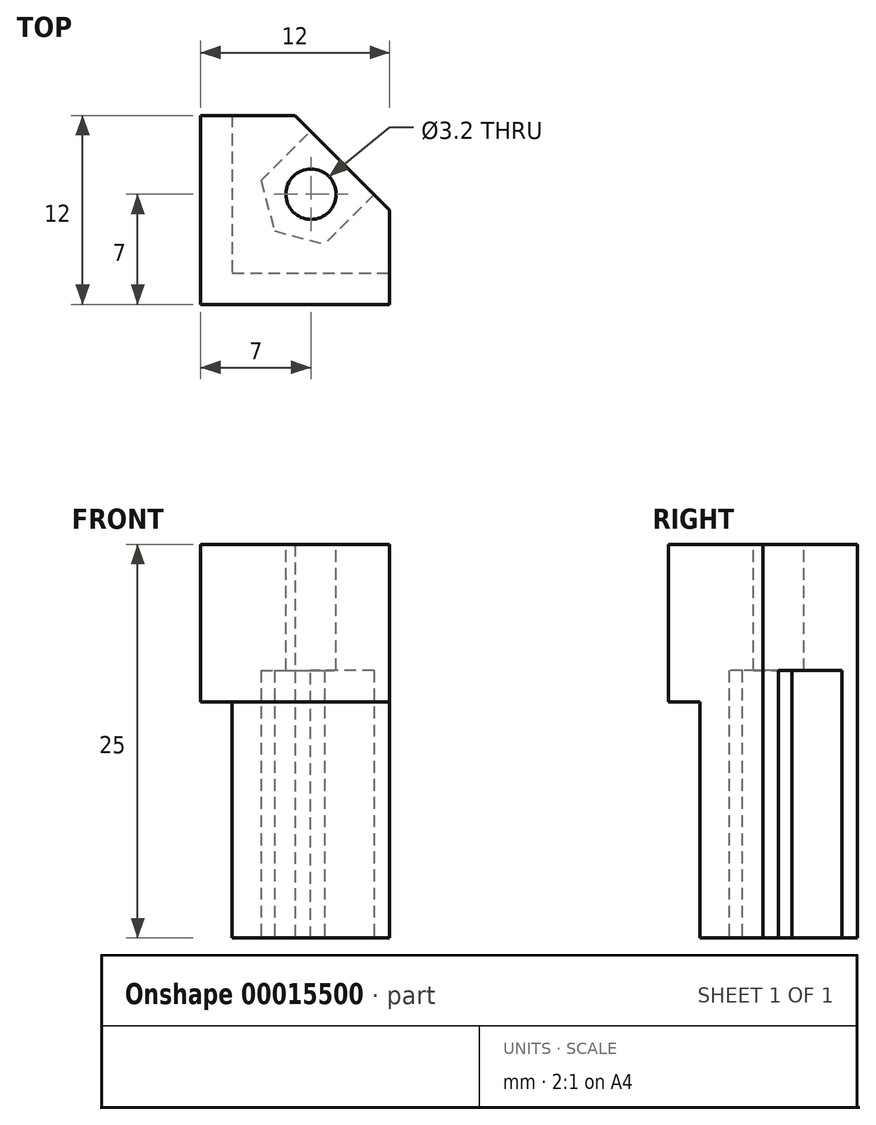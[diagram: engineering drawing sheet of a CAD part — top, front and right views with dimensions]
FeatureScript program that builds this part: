
annotation { "Feature Type Name" : "Feature", "Feature Type Description" : "" }
export const myFeature = defineFeature(function(context is Context, id is Id, definition is map)
    precondition{}
    {
        {
            var Q0;
            Q0=qCreatedBy(makeId("Top.planeOp"),FACE);
            var sketch = newSketch(context, id + "F0", { "sketchPlane" : qUnion([Q0])});
            skLineSegment(sketch, "E0", {"start": v(0, 0) * mm, "end": v(0, 12) * mm});
            skLineSegment(sketch, "E1", {"start": v(0, 12) * mm, "end": v(6, 12) * mm});
            skLineSegment(sketch, "E2", {"start": v(6, 12) * mm, "end": v(12, 6) * mm});
            skLineSegment(sketch, "E3", {"start": v(12, 6) * mm, "end": v(12, 0) * mm});
            skLineSegment(sketch, "E4", {"start": v(12, 0) * mm, "end": v(0, 0) * mm});
            skSolve(sketch);
        }
        {
            var Q0;
            Q0 = qSketchRegion(id + "F0", true);
            extrude(context, id + "F1", {"entities" : qUnion([Q0]), "depth" : 10 * mm});
        }
        {
            var Q0;
            Q0=qCreatedBy(makeId("Top.planeOp"),FACE);
            var sketch = newSketch(context, id + "F2", { "sketchPlane" : qUnion([Q0])});
            skLineSegment(sketch, "E5", {"start": v(2, 12) * mm, "end": v(2, 2) * mm});
            skLineSegment(sketch, "E6", {"start": v(2, 2) * mm, "end": v(12, 2) * mm});
            skLineSegment(sketch, "E7", {"start": v(12, 2) * mm, "end": v(2, 12) * mm, "construction": true});
            skLineSegment(sketch, "E8", {"start": v(12, 2) * mm, "end": v(12, 6) * mm});
            skLineSegment(sketch, "E9", {"start": v(12, 6) * mm, "end": v(6, 12) * mm});
            skLineSegment(sketch, "E10", {"start": v(6, 12) * mm, "end": v(2, 12) * mm});
            skSolve(sketch);
        }
        {
            var Q0;
            Q0 = qSketchRegion(id + "F2", true);
            extrude(context, id + "F3", {"entities" : qUnion([Q0]), "operationType" : NewBodyOperationType.ADD, "oppositeDirection" : true, "depth" : 15 * mm});
        }
        {
            var Q0;
            Q0=makeQuery(id+"F1.opExtrude","CAP_FACE",FACE,{"disambiguationData":[OSD([sQuery(id+"F0.wireOp",EDGE,"E0"),sQuery(id+"F0.wireOp",EDGE,"E1"),sQuery(id+"F0.wireOp",EDGE,"E2"),sQuery(id+"F0.wireOp",EDGE,"E3"),sQuery(id+"F0.wireOp",EDGE,"E4")])],"isStart":false});
            var sketch = newSketch(context, id + "F4", { "sketchPlane" : qUnion([Q0])});
            skPoint(sketch, "E11", {"position": v(7, 7) * mm});
            skSolve(sketch);
        }
        {
            var Q0;
            Q0=sQuery(id+"F4.wireOp",VERTEX,"E11");
            var Q1;
            Q1=makeQuery(id+"F1.opExtrude","SWEPT_BODY",BODY,{"disambiguationData":[OSD([sQuery(id+"F0.wireOp",EDGE,"E0"),sQuery(id+"F0.wireOp",EDGE,"E1"),sQuery(id+"F0.wireOp",EDGE,"E2"),sQuery(id+"F0.wireOp",EDGE,"E3"),sQuery(id+"F0.wireOp",EDGE,"E4")])]});
            hole(context, id + "F5", {"style" : HoleStyle.SIMPLE, "holeDiameter" : 3.2 * mm, "endStyle" : HoleEndStyle.THROUGH, "locations" : qUnion([Q0]), "scope" : qUnion([Q1])});
        }
        {
            var Q0;
            Q0=makeQuery(id+"F3.opExtrude","CAP_FACE",FACE,{"disambiguationData":[OSD([sQuery(id+"F2.wireOp",EDGE,"E5"),sQuery(id+"F2.wireOp",EDGE,"E6"),sQuery(id+"F2.wireOp",EDGE,"E7")])],"isStart":false});
            var sketch = newSketch(context, id + "F6", { "sketchPlane" : qUnion([Q0])});
            skCircle(sketch, "E12.cCircle", {"center": v(7, -7) * mm, "radius": 2.85 * mm, "construction": true});
            skLineSegment(sketch, "E12.0", {"start": v(6.15, -10.18) * mm, "end": v(3.82, -7.85) * mm});
            skLineSegment(sketch, "E12.1", {"start": v(3.82, -7.85) * mm, "end": v(4.67, -4.67) * mm});
            skLineSegment(sketch, "E12.2", {"start": v(4.67, -4.67) * mm, "end": v(7.85, -3.82) * mm});
            skLineSegment(sketch, "E12.3", {"start": v(7.85, -3.82) * mm, "end": v(10.18, -6.15) * mm});
            skLineSegment(sketch, "E12.4", {"start": v(10.18, -6.15) * mm, "end": v(9.33, -9.33) * mm, "construction": true});
            skLineSegment(sketch, "E12.5", {"start": v(9.33, -9.33) * mm, "end": v(6.15, -10.18) * mm, "construction": true});
            skPoint(sketch, "E12.0.midPoint", {"position": v(4.98, -9.02) * mm});
            skLineSegment(sketch, "E13", {"start": v(0, 0) * mm, "end": v(7, -7) * mm, "construction": true});
            skLineSegment(sketch, "E14", {"start": v(6.15, -10.18) * mm, "end": v(7.31, -11.34) * mm});
            skLineSegment(sketch, "E15", {"start": v(7.31, -11.34) * mm, "end": v(9.33, -9.33) * mm});
            skLineSegment(sketch, "E16", {"start": v(9.33, -9.33) * mm, "end": v(11.34, -7.31) * mm});
            skLineSegment(sketch, "E17", {"start": v(11.34, -7.31) * mm, "end": v(10.18, -6.15) * mm});
            skSolve(sketch);
        }
        {
            var Q0;
            Q0 = qSketchRegion(id + "F6", true);
            extrude(context, id + "F7", {"entities" : qUnion([Q0]), "operationType" : NewBodyOperationType.REMOVE, "oppositeDirection" : true, "depth" : 17 * mm});
        }
    });
